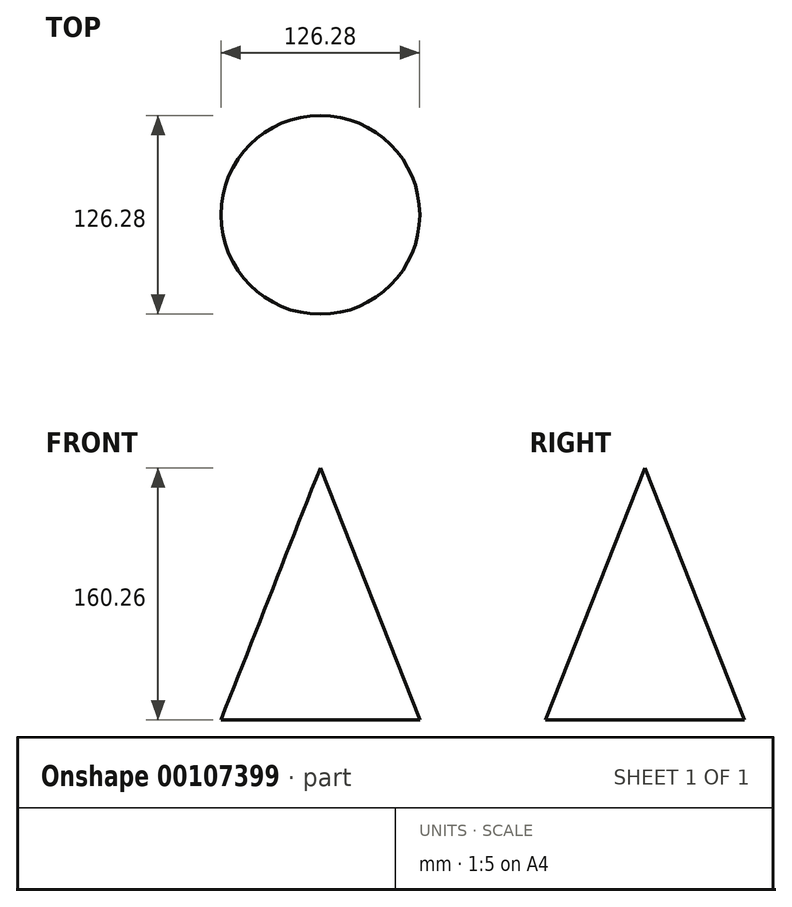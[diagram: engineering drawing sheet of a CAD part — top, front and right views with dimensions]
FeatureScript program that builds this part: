
annotation { "Feature Type Name" : "Feature", "Feature Type Description" : "" }
export const myFeature = defineFeature(function(context is Context, id is Id, definition is map)
    precondition{}
    {
        {
            var Q0;
            Q0=qCreatedBy(makeId("Top.planeOp"),FACE);
            var sketch = newSketch(context, id + "F0", { "sketchPlane" : qUnion([Q0])});
            skCircle(sketch, "E0", {"center": v(0, 0) * mm, "radius": 63.14 * mm});
            skSolve(sketch);
        }
        {
            var Q0;
            Q0=qCreatedBy(makeId("Front.planeOp"),FACE);
            var sketch = newSketch(context, id + "F1", { "sketchPlane" : qUnion([Q0])});
            skLineSegment(sketch, "E1", {"start": v(0, 0) * mm, "end": v(0, 160.26) * mm});
            skSolve(sketch);
        }
        {
            var Q0;
            Q0=makeQuery(id+"F0.imprint","IMPRINT",FACE,{"disambiguationData":[TD([[makeQuery(id+"F0.imprint","IMPRINT",EDGE,{"derivedFrom":sQuery(id+"F0.wireOp",EDGE,"E0")}),1.0]])]});
            var Q1;
            Q1=sQuery(id+"F1.wireOp",VERTEX,"E1.end");
            loft(context, id + "F2", {"sheetProfilesArray" : [{ "sheetProfileEntities" : qUnion([Q0]) }, { "sheetProfileEntities" : qUnion([Q1]) }]});
        }
    });
